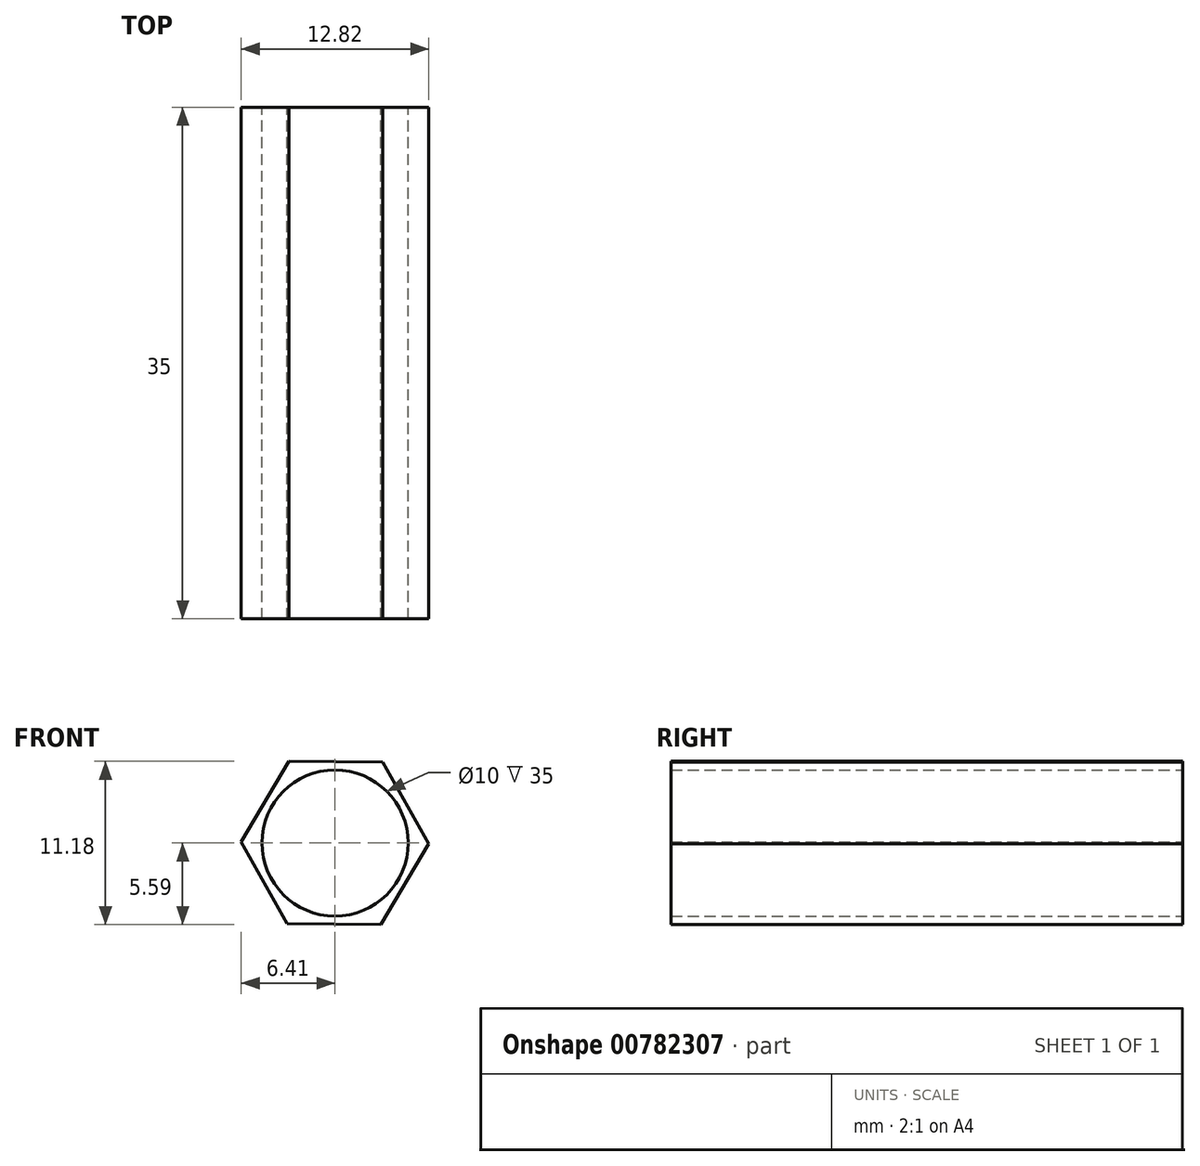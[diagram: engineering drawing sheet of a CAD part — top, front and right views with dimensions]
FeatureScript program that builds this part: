
annotation { "Feature Type Name" : "Feature", "Feature Type Description" : "" }
export const myFeature = defineFeature(function(context is Context, id is Id, definition is map)
    precondition{}
    {
        {
            var Q0;
            Q0=qCreatedBy(makeId("Front.planeOp"),FACE);
            var sketch = newSketch(context, id + "F0", { "sketchPlane" : qUnion([Q0])});
            skCircle(sketch, "E0.cCircle", {"center": v(0, 0) * mm, "radius": 5.55 * mm, "construction": true});
            skLineSegment(sketch, "E0.0", {"start": v(-6.41, 0.07) * mm, "end": v(-3.15, 5.59) * mm});
            skLineSegment(sketch, "E0.1", {"start": v(-3.15, 5.59) * mm, "end": v(3.27, 5.52) * mm});
            skLineSegment(sketch, "E0.2", {"start": v(3.27, 5.52) * mm, "end": v(6.41, -0.07) * mm});
            skLineSegment(sketch, "E0.3", {"start": v(6.41, -0.07) * mm, "end": v(3.15, -5.59) * mm});
            skLineSegment(sketch, "E0.4", {"start": v(3.15, -5.59) * mm, "end": v(-3.27, -5.52) * mm});
            skLineSegment(sketch, "E0.5", {"start": v(-3.27, -5.52) * mm, "end": v(-6.41, 0.07) * mm});
            skPoint(sketch, "E0.0.midPoint", {"position": v(-4.78, 2.83) * mm});
            skCircle(sketch, "E1", {"center": v(0, 0) * mm, "radius": 5 * mm});
            skSolve(sketch);
        }
        {
            var Q0;
            Q0 = qSketchRegion(id + "F0", true);
            extrude(context, id + "F1", {"entities" : qUnion([Q0]), "depth" : 35 * mm, "offsetDistance" : 25 * mm});
        }
    });
